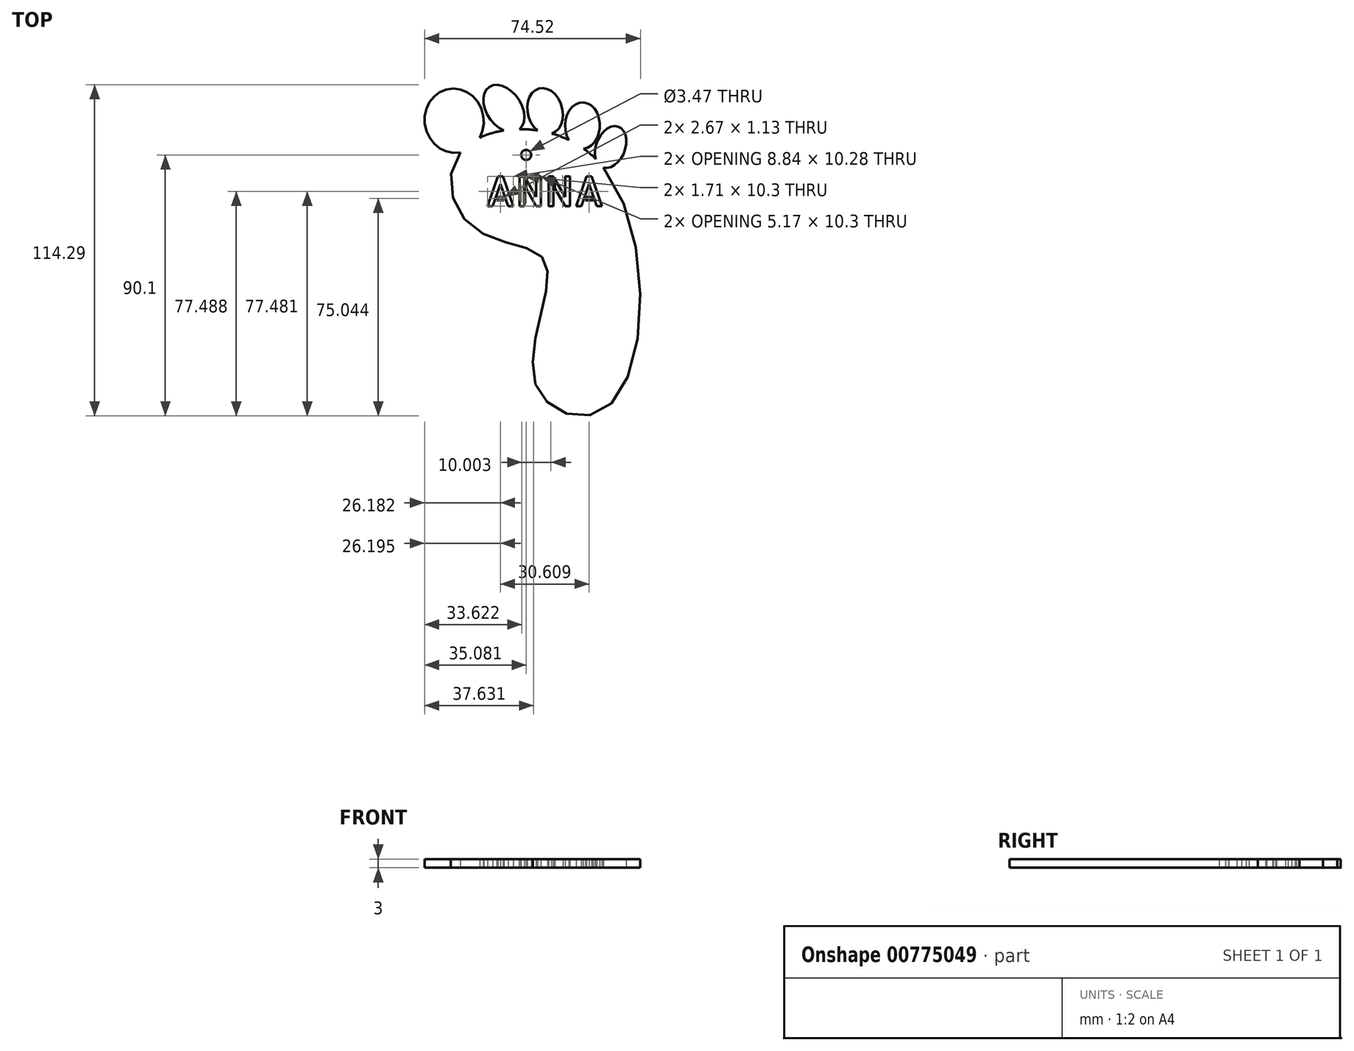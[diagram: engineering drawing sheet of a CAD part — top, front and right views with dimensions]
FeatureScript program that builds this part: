
annotation { "Feature Type Name" : "Feature", "Feature Type Description" : "" }
export const myFeature = defineFeature(function(context is Context, id is Id, definition is map)
    precondition{}
    {
        {
            var Q0;
            Q0=qCreatedBy(makeId("Top.planeOp"),FACE);
            var sketch = newSketch(context, id + "F0", { "sketchPlane" : qUnion([Q0])});
            skFitSpline(sketch, "E0", {"points": [v(-27.97, 35.88) * mm, v(19.79, 32.6) * mm, v(23.88, -51.17) * mm, v(0, -48.07) * mm, v(0, -19.63) * mm, v(0, 0) * mm, v(-23.6, 9.96) * mm, v(-27.97, 35.88) * mm]});
            skEllipse(sketch, "E1", {"center": v(-30.06, 46.8) * mm, "majorRadius": 11.11 * mm, "minorRadius": 10.2 * mm, "majorAxis": v(0.19, -0.98)});
            skEllipse(sketch, "E2", {"center": v(-12.9, 51.03) * mm, "majorRadius": 9 * mm, "minorRadius": 6 * mm, "majorAxis": v(0.56, -0.83)});
            skEllipse(sketch, "E3", {"center": v(1.31, 50.09) * mm, "majorRadius": 8.1 * mm, "minorRadius": 6.01 * mm, "majorAxis": v(0.26, -0.96)});
            skEllipse(sketch, "E4", {"center": v(14.22, 45.13) * mm, "majorRadius": 8 * mm, "minorRadius": 6 * mm, "majorAxis": v(0, -1)});
            skEllipse(sketch, "E5", {"center": v(23.96, 37.74) * mm, "majorRadius": 7.5 * mm, "minorRadius": 5 * mm, "majorAxis": v(-0.37, -0.93)});
            skText(sketch, "E6", { "text": "ANNA", "fontName": "AllertaStencil-Regular.ttf"});
            skCircle(sketch, "E7", {"center": v(-5.2, 35) * mm, "radius": 1.74 * mm});
            const initialGuessF0  = {"E6": [-0.01941, 0.01724, 1, 0, 0.0103]};
            skSetInitialGuess(sketch, initialGuessF0);
            skSolve(sketch);
        }
        {
            var Q0;
            Q0 = qSketchRegion(id + "F0", true);
            extrude(context, id + "F1", {"entities" : qUnion([Q0]), "flatOperationType" : FlatOperationType.REMOVE, "depth" : 3 * mm, "offsetDistance" : 25 * mm, "domain" : OperationDomain.MODEL});
        }
    });
